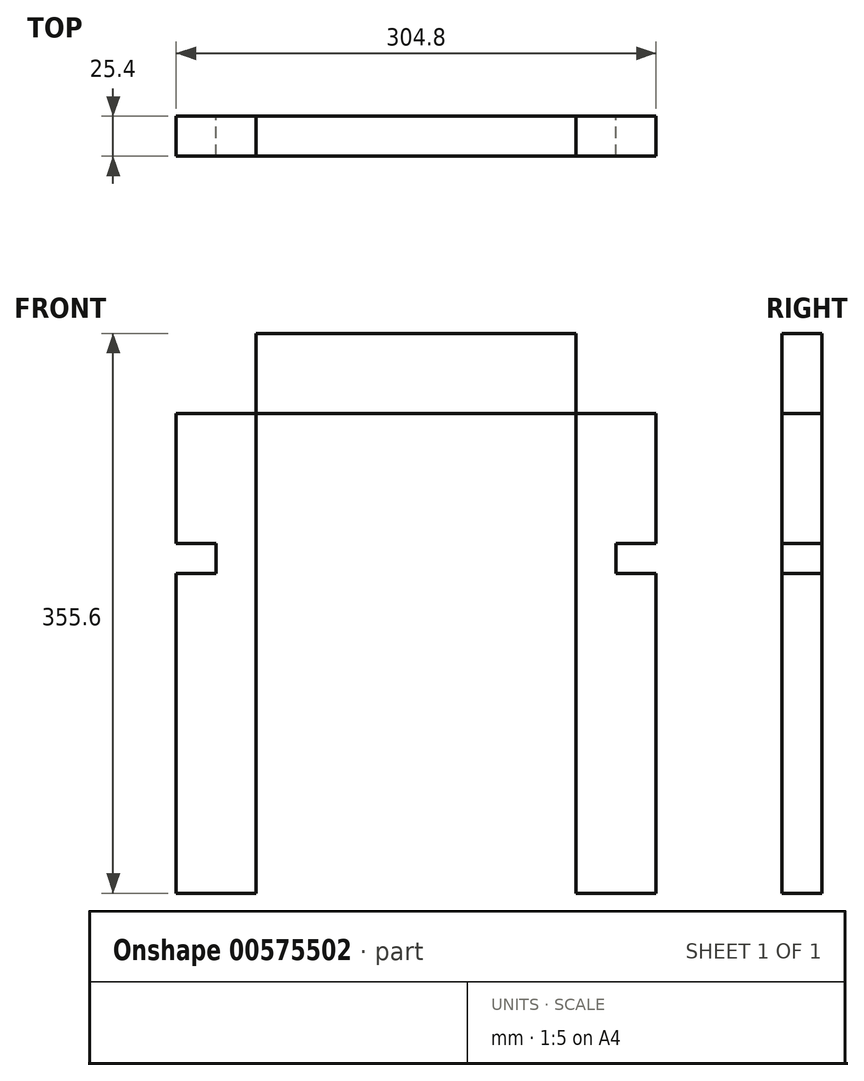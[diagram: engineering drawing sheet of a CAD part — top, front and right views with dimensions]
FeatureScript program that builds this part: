
annotation { "Feature Type Name" : "Feature", "Feature Type Description" : "" }
export const myFeature = defineFeature(function(context is Context, id is Id, definition is map)
    precondition{}
    {
        {
            var Q0;
            Q0=qCreatedBy(makeId("Front.planeOp"),FACE);
            var sketch = newSketch(context, id + "F0", { "sketchPlane" : qUnion([Q0])});
            skLineSegment(sketch, "E0.bottom", {"start": v(83.38, -355.6) * mm, "end": v(32.58, -355.6) * mm});
            skLineSegment(sketch, "E0.top", {"start": v(83.38, 0) * mm, "end": v(32.58, 0) * mm});
            skLineSegment(sketch, "E0.left", {"start": v(83.38, -355.6) * mm, "end": v(83.38, 0) * mm});
            skLineSegment(sketch, "E0.right", {"start": v(32.58, -355.6) * mm, "end": v(32.58, 0) * mm});
            skLineSegment(sketch, "E1.bottom", {"start": v(-170.62, 0) * mm, "end": v(-221.42, 0) * mm});
            skLineSegment(sketch, "E1.top", {"start": v(-170.62, -355.6) * mm, "end": v(-221.42, -355.6) * mm});
            skLineSegment(sketch, "E1.left", {"start": v(-170.62, 0) * mm, "end": v(-170.62, -355.6) * mm});
            skLineSegment(sketch, "E1.right", {"start": v(-221.42, 0) * mm, "end": v(-221.42, -355.6) * mm});
            skLineSegment(sketch, "E2.bottom", {"start": v(83.38, 0) * mm, "end": v(-221.42, 0) * mm});
            skLineSegment(sketch, "E2.top", {"start": v(83.38, -50.8) * mm, "end": v(-221.42, -50.8) * mm});
            skLineSegment(sketch, "E2.left", {"start": v(83.38, 0) * mm, "end": v(83.38, -50.8) * mm});
            skLineSegment(sketch, "E2.right", {"start": v(-221.42, 0) * mm, "end": v(-221.42, -50.8) * mm});
            skPoint(sketch, "E3.middle", {"position": v(-69.02, 0) * mm});
            skLineSegment(sketch, "E4.bottom", {"start": v(-30.92, -25.4) * mm, "end": v(-107.12, -25.4) * mm});
            skLineSegment(sketch, "E4.top", {"start": v(-30.92, 25.4) * mm, "end": v(-107.12, 25.4) * mm});
            skLineSegment(sketch, "E4.left", {"start": v(-30.92, -25.4) * mm, "end": v(-30.92, 25.4) * mm});
            skLineSegment(sketch, "E4.right", {"start": v(-107.12, -25.4) * mm, "end": v(-107.12, 25.4) * mm});
            skLineSegment(sketch, "E5.bottom", {"start": v(-30.92, -25.4) * mm, "end": v(-49.97, -25.4) * mm});
            skLineSegment(sketch, "E5.top", {"start": v(-30.92, 38.1) * mm, "end": v(-49.97, 38.1) * mm});
            skLineSegment(sketch, "E5.left", {"start": v(-30.92, -25.4) * mm, "end": v(-30.92, 38.1) * mm});
            skLineSegment(sketch, "E5.right", {"start": v(-49.97, -25.4) * mm, "end": v(-49.97, 38.1) * mm});
            skLineSegment(sketch, "E6.bottom", {"start": v(-107.12, -25.4) * mm, "end": v(-88.07, -25.4) * mm});
            skLineSegment(sketch, "E6.top", {"start": v(-107.12, 38.1) * mm, "end": v(-88.07, 38.1) * mm});
            skLineSegment(sketch, "E6.left", {"start": v(-107.12, -25.4) * mm, "end": v(-107.12, 38.1) * mm});
            skLineSegment(sketch, "E6.right", {"start": v(-88.07, -25.4) * mm, "end": v(-88.07, 38.1) * mm});
            skLineSegment(sketch, "E7.bottom", {"start": v(83.38, -133.35) * mm, "end": v(57.98, -133.35) * mm});
            skLineSegment(sketch, "E7.top", {"start": v(83.38, -152.4) * mm, "end": v(57.98, -152.4) * mm});
            skLineSegment(sketch, "E7.left", {"start": v(83.38, -133.35) * mm, "end": v(83.38, -152.4) * mm});
            skLineSegment(sketch, "E7.right", {"start": v(57.98, -133.35) * mm, "end": v(57.98, -152.4) * mm});
            skLineSegment(sketch, "E8.bottom", {"start": v(-221.42, -152.4) * mm, "end": v(-196.02, -152.4) * mm});
            skLineSegment(sketch, "E8.top", {"start": v(-221.42, -133.35) * mm, "end": v(-196.02, -133.35) * mm});
            skLineSegment(sketch, "E8.left", {"start": v(-221.42, -152.4) * mm, "end": v(-221.42, -133.35) * mm});
            skLineSegment(sketch, "E8.right", {"start": v(-196.02, -152.4) * mm, "end": v(-196.02, -133.35) * mm});
            skSolve(sketch);
        }
        {
            var Q0;
            {var subQ5=sQuery(id+"F0.wireOp",EDGE,"E2.right");Q0=makeQuery(id+"F0.imprint","IMPRINT",FACE,{"disambiguationData":[TD([[makeQuery(id+"F0.imprint","IMPRINT",EDGE,{"derivedFrom":subQ5}),1.0]])]});}
            var Q1;
            {var subQ12=sQuery(id+"F0.wireOp",EDGE,"E3.top");Q1=makeQuery(id+"F0.imprint","IMPRINT",FACE,{"disambiguationData":[TD([[makeQuery(id+"F0.imprint","IMPRINT",EDGE,{"derivedFrom":subQ12}),-1.0]])]});}
            var Q2;
            {var subQ5=sQuery(id+"F0.wireOp",EDGE,"E2.left");Q2=makeQuery(id+"F0.imprint","IMPRINT",FACE,{"disambiguationData":[TD([[makeQuery(id+"F0.imprint","IMPRINT",EDGE,{"derivedFrom":subQ5}),-1.0]])]});}
            var Q3;
            {var subQ0=sQuery(id+"F0.wireOp",EDGE,"E0.bottom");Q3=makeQuery(id+"F0.imprint","IMPRINT",FACE,{"disambiguationData":[TD([[makeQuery(id+"F0.imprint","IMPRINT",EDGE,{"derivedFrom":subQ0}),-1.0]])]});}
            var Q4;
            {var subQ0=sQuery(id+"F0.wireOp",EDGE,"E1.top");Q4=makeQuery(id+"F0.imprint","IMPRINT",FACE,{"disambiguationData":[TD([[makeQuery(id+"F0.imprint","IMPRINT",EDGE,{"derivedFrom":subQ0}),-1.0]])]});}
            var Q5;
            Q5=makeQuery(id+"F0.imprint","IMPRINT",FACE,{"disambiguationData":[TD([[makeQuery(id+"F0.imprint","IMPRINT",EDGE,{"derivedFrom":sQuery(id+"F0.wireOp",EDGE,"E4.bottom")}),1.0]])]});
            var Q6;
            {var subQ5=sQuery(id+"F0.wireOp",EDGE,"E4.bottom");Q6=makeQuery(id+"F0.imprint","IMPRINT",FACE,{"disambiguationData":[TD([[makeQuery(id+"F0.imprint","IMPRINT",EDGE,{"derivedFrom":subQ5}),-1.0]])]});}
            extrude(context, id + "F1", {"entities" : qUnion([Q0, Q1, Q2, Q3, Q4, Q5, Q6]), "depth" : 25.4 * mm, "offsetDistance" : 25.4 * mm});
        }
    });
